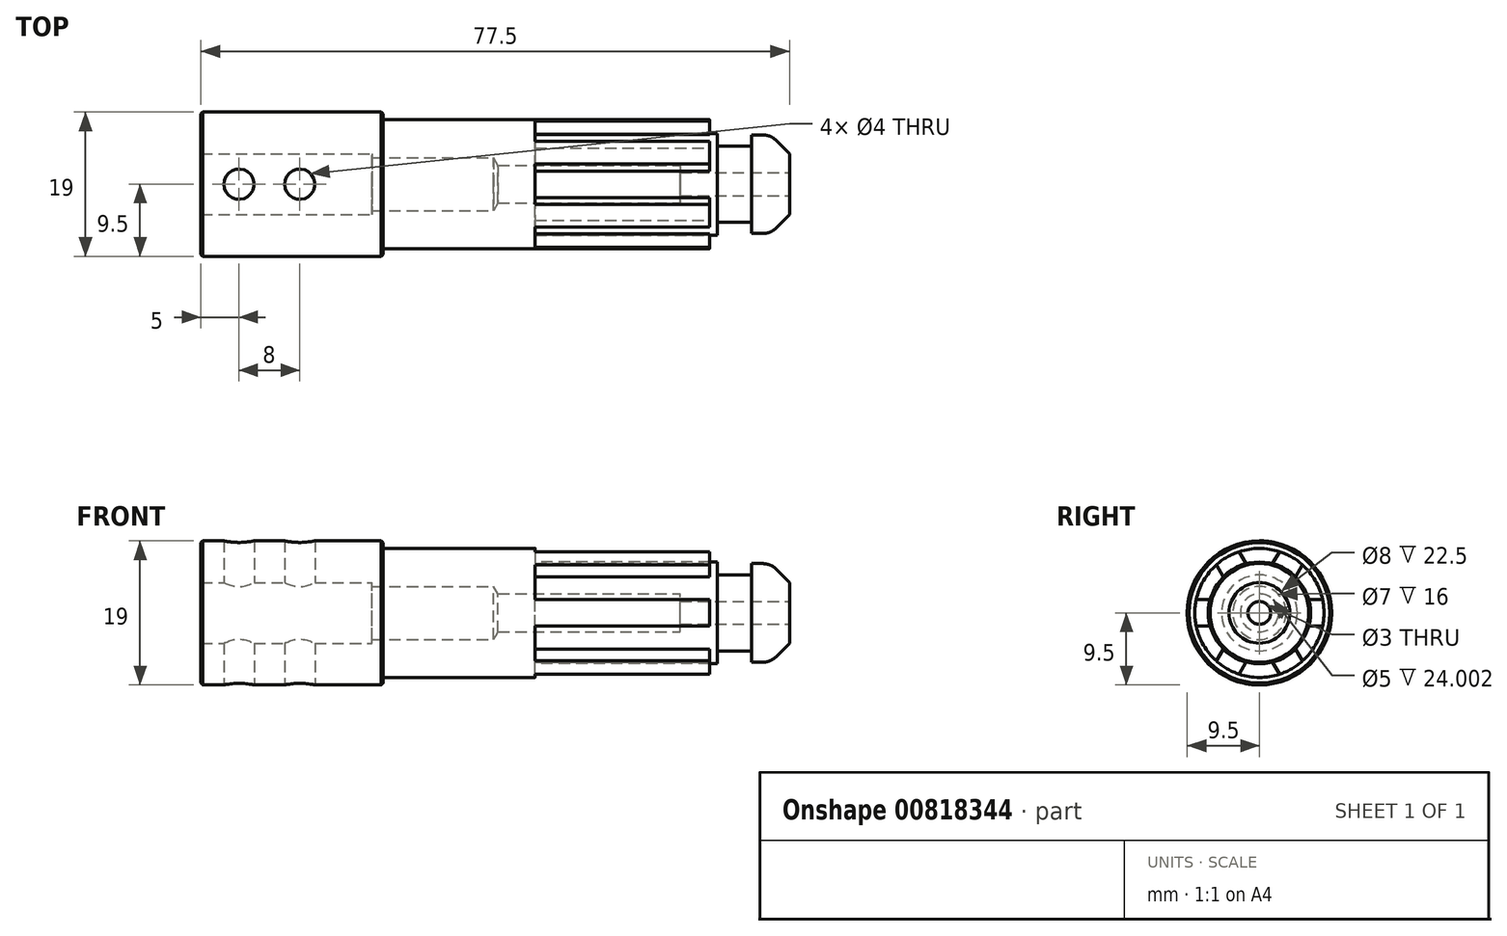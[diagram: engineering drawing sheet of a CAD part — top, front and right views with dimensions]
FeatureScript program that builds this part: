
annotation { "Feature Type Name" : "Feature", "Feature Type Description" : "" }
export const myFeature = defineFeature(function(context is Context, id is Id, definition is map)
    precondition{}
    {
        {
            var Q0;
            Q0=qCreatedBy(makeId("Right.planeOp"),FACE);
            var sketch = newSketch(context, id + "F0", { "sketchPlane" : qUnion([Q0])});
            skCircle(sketch, "E0", {"center": v(0, 0) * mm, "radius": 9.5 * mm});
            skSolve(sketch);
        }
        {
            var Q0;
            Q0=makeQuery(id+"F0.imprint","IMPRINT",FACE,{"disambiguationData":[TD([[makeQuery(id+"F0.imprint","IMPRINT",EDGE,{"derivedFrom":sQuery(id+"F0.wireOp",EDGE,"E0")}),1.0]])]});
            extrude(context, id + "F1", {"entities" : qUnion([Q0]), "depth" : 24 * mm, "offsetDistance" : 25 * mm});
        }
        {
            var Q0;
            Q0=makeQuery(id+"F1.opExtrude","CAP_FACE",FACE,{"disambiguationData":[OSD([sQuery(id+"F0.wireOp",EDGE,"E0")])],"isStart":false});
            var sketch = newSketch(context, id + "F2", { "sketchPlane" : qUnion([Q0])});
            skCircle(sketch, "E1", {"center": v(0, 0) * mm, "radius": 8.5 * mm});
            skSolve(sketch);
        }
        {
            var Q0;
            Q0=makeQuery(id+"F2.imprint","IMPRINT",FACE,{"disambiguationData":[TD([[makeQuery(id+"F2.imprint","IMPRINT",EDGE,{"derivedFrom":sQuery(id+"F2.wireOp",EDGE,"E1")}),1.0]])]});
            extrude(context, id + "F3", {"entities" : qUnion([Q0]), "operationType" : NewBodyOperationType.ADD, "depth" : 43 * mm, "offsetDistance" : 25 * mm});
        }
        {
            var Q0;
            Q0=makeQuery(id+"F3.opExtrude","CAP_FACE",FACE,{"disambiguationData":[OSD([sQuery(id+"F2.wireOp",EDGE,"E1")])],"isStart":false});
            var sketch = newSketch(context, id + "F4", { "sketchPlane" : qUnion([Q0])});
            skCircle(sketch, "E2", {"center": v(0, 0) * mm, "radius": 6.7 * mm});
            skSolve(sketch);
        }
        {
            var Q0;
            Q0=makeQuery(id+"F4.imprint","IMPRINT",FACE,{"disambiguationData":[TD([[makeQuery(id+"F4.imprint","IMPRINT",EDGE,{"derivedFrom":sQuery(id+"F4.wireOp",EDGE,"E2")}),1.0]])]});
            extrude(context, id + "F5", {"entities" : qUnion([Q0]), "operationType" : NewBodyOperationType.ADD, "depth" : 1 * mm, "offsetDistance" : 25 * mm});
        }
        {
            var Q0;
            Q0=makeQuery(id+"F5.opExtrude","CAP_FACE",FACE,{"disambiguationData":[OSD([sQuery(id+"F4.wireOp",EDGE,"E2")])],"isStart":false});
            var sketch = newSketch(context, id + "F6", { "sketchPlane" : qUnion([Q0])});
            skCircle(sketch, "E3", {"center": v(0, 0) * mm, "radius": 5 * mm});
            skSolve(sketch);
        }
        {
            var Q0;
            Q0=makeQuery(id+"F6.imprint","IMPRINT",FACE,{"disambiguationData":[TD([[makeQuery(id+"F6.imprint","IMPRINT",EDGE,{"derivedFrom":sQuery(id+"F6.wireOp",EDGE,"E3")}),1.0]])]});
            extrude(context, id + "F7", {"entities" : qUnion([Q0]), "operationType" : NewBodyOperationType.ADD, "depth" : 4.5 * mm, "offsetDistance" : 25 * mm});
        }
        {
            var Q0;
            Q0=makeQuery(id+"F7.opExtrude","CAP_FACE",FACE,{"disambiguationData":[OSD([sQuery(id+"F6.wireOp",EDGE,"E3")])],"isStart":false});
            var sketch = newSketch(context, id + "F8", { "sketchPlane" : qUnion([Q0])});
            skCircle(sketch, "E4", {"center": v(0, 0) * mm, "radius": 6.5 * mm});
            skSolve(sketch);
        }
        {
            var Q0;
            Q0=makeQuery(id+"F8.imprint","IMPRINT",FACE,{"disambiguationData":[TD([[makeQuery(id+"F8.imprint","IMPRINT",EDGE,{"derivedFrom":sQuery(id+"F8.wireOp",EDGE,"E4")}),1.0]])]});
            var Q1;
            Q1=makeQuery(id+"F8.imprint","IMPRINT",FACE,{"disambiguationData":[TD([[makeQuery(id+"F8.imprint","IMPRINT",EDGE,{"derivedFrom":makeQuery(id+"F7.opExtrude","CAP_EDGE",EDGE,{"disambiguationData":[OSD([sQuery(id+"F6.wireOp",EDGE,"E3")])],"isStart":false})}),1.0]])]});
            extrude(context, id + "F9", {"entities" : qUnion([Q0, Q1]), "operationType" : NewBodyOperationType.ADD, "depth" : 5 * mm, "offsetDistance" : 25 * mm});
        }
        {
            var Q0;
            Q0=makeQuery(id+"F9.opExtrude","CAP_EDGE",EDGE,{"disambiguationData":[OSD([sQuery(id+"F8.wireOp",EDGE,"E4")])],"isStart":false});
            chamfer(context, id + "F10", {"entities" : qUnion([Q0]), "width" : 2.5 * mm, "tangentPropagation" : true});
        }
        {
            var Q0;
            {var subQ0=sQuery(id+"F8.wireOp",EDGE,"E4");Q0=makeQuery(id+"F10.opChamfer","BLEND_EDGE",EDGE,{"blendedFrom":[makeQuery(id+"F9.opExtrude","CAP_EDGE",EDGE,{"disambiguationData":[OSD([subQ0])],"isStart":false}),makeQuery(id+"F9.opExtrude","SWEPT_FACE",FACE,{"disambiguationData":[OSD([subQ0])]})],"blendedInto":[makeQuery(id+"F9.opExtrude","SWEPT_FACE",FACE,{"disambiguationData":[OSD([subQ0])]})]});}
            fillet(context, id + "F11", {"entities" : qUnion([Q0]), "radius" : 2.5 * mm, "tangentPropagation" : true, "allowEdgeOverflow" : false});
        }
        {
            var Q0;
            Q0=makeQuery(id+"F3.opExtrude","CAP_FACE",FACE,{"disambiguationData":[OSD([sQuery(id+"F2.wireOp",EDGE,"E1")])],"isStart":false});
            var sketch = newSketch(context, id + "F12", { "sketchPlane" : qUnion([Q0])});
            skArc(sketch, "E5", {"start": v(-1.74, 6.52) * mm, "mid": v(-3.37, 5.85) * mm, "end": v(-4.78, 4.77) * mm});
            skLineSegment(sketch, "E6", {"start": v(9.02, 1.75) * mm, "end": v(6.52, 1.75) * mm});
            skLineSegment(sketch, "E7", {"start": v(9.02, -1.75) * mm, "end": v(6.47, -1.75) * mm});
            skLineSegment(sketch, "E8.1.0", {"start": v(3, 8.69) * mm, "end": v(1.74, 6.52) * mm});
            skLineSegment(sketch, "E8.1.3", {"start": v(6.03, 6.94) * mm, "end": v(4.75, 4.73) * mm});
            skLineSegment(sketch, "E8.2.0", {"start": v(-6.03, 6.94) * mm, "end": v(-4.78, 4.77) * mm});
            skLineSegment(sketch, "E8.2.3", {"start": v(-3, 8.69) * mm, "end": v(-1.72, 6.48) * mm});
            skLineSegment(sketch, "E8.3.0", {"start": v(-9.02, -1.75) * mm, "end": v(-6.52, -1.75) * mm});
            skLineSegment(sketch, "E8.3.3", {"start": v(-9.02, 1.75) * mm, "end": v(-6.47, 1.75) * mm});
            skLineSegment(sketch, "E8.4.0", {"start": v(-3, -8.69) * mm, "end": v(-1.74, -6.52) * mm});
            skLineSegment(sketch, "E8.4.3", {"start": v(-6.03, -6.94) * mm, "end": v(-4.75, -4.73) * mm});
            skLineSegment(sketch, "E8.5.0", {"start": v(6.03, -6.94) * mm, "end": v(4.78, -4.77) * mm});
            skLineSegment(sketch, "E8.5.3", {"start": v(3, -8.69) * mm, "end": v(1.72, -6.48) * mm});
            skLineSegment(sketch, "E9", {"start": v(-3, 8.69) * mm, "end": v(3, 8.69) * mm});
            skLineSegment(sketch, "E10", {"start": v(6.03, 6.94) * mm, "end": v(9.02, 1.75) * mm});
            skLineSegment(sketch, "E11", {"start": v(9.02, -1.75) * mm, "end": v(6.03, -6.94) * mm});
            skLineSegment(sketch, "E12", {"start": v(3, -8.69) * mm, "end": v(-3, -8.69) * mm});
            skLineSegment(sketch, "E13", {"start": v(-6.03, -6.94) * mm, "end": v(-9.02, -1.75) * mm});
            skLineSegment(sketch, "E14", {"start": v(-9.02, 1.75) * mm, "end": v(-6.03, 6.94) * mm});
            skArc(sketch, "E15.trimOffspring", {"start": v(4.78, 4.77) * mm, "mid": v(3.38, 5.85) * mm, "end": v(1.74, 6.52) * mm});
            skArc(sketch, "E16.trimOffspring", {"start": v(6.52, -1.75) * mm, "mid": v(6.75, 0) * mm, "end": v(6.52, 1.75) * mm});
            skArc(sketch, "E17.trimOffspring", {"start": v(1.74, -6.52) * mm, "mid": v(3.38, -5.85) * mm, "end": v(4.78, -4.77) * mm});
            skArc(sketch, "E18.trimOffspring", {"start": v(-4.78, -4.77) * mm, "mid": v(-3.38, -5.85) * mm, "end": v(-1.74, -6.52) * mm});
            skArc(sketch, "E19.trimOffspring", {"start": v(-6.52, 1.75) * mm, "mid": v(-6.75, 0) * mm, "end": v(-6.52, -1.75) * mm});
            skSolve(sketch);
        }
        {
            var Q0;
            {var subQ5=sQuery(id+"F12.wireOp",EDGE,"E5");Q0=makeQuery(id+"F12.imprint","IMPRINT",FACE,{"disambiguationData":[TD([[makeQuery(id+"F12.imprint","IMPRINT",EDGE,{"derivedFrom":subQ5}),1.0]])]});}
            var Q1;
            {var subQ10=sQuery(id+"F12.wireOp",EDGE,"E19.trimOffspring");Q1=makeQuery(id+"F12.imprint","IMPRINT",FACE,{"disambiguationData":[TD([[makeQuery(id+"F12.imprint","IMPRINT",EDGE,{"derivedFrom":subQ10}),1.0]])]});}
            var Q2;
            {var subQ4=sQuery(id+"F12.wireOp",EDGE,"E18.trimOffspring");Q2=makeQuery(id+"F12.imprint","IMPRINT",FACE,{"disambiguationData":[TD([[makeQuery(id+"F12.imprint","IMPRINT",EDGE,{"derivedFrom":subQ4}),1.0]])]});}
            var Q3;
            {var subQ10=sQuery(id+"F12.wireOp",EDGE,"E16.trimOffspring");Q3=makeQuery(id+"F12.imprint","IMPRINT",FACE,{"disambiguationData":[TD([[makeQuery(id+"F12.imprint","IMPRINT",EDGE,{"derivedFrom":subQ10}),1.0]])]});}
            var Q4;
            {var subQ6=sQuery(id+"F12.wireOp",EDGE,"E15.trimOffspring");Q4=makeQuery(id+"F12.imprint","IMPRINT",FACE,{"disambiguationData":[TD([[makeQuery(id+"F12.imprint","IMPRINT",EDGE,{"derivedFrom":subQ6}),1.0]])]});}
            var Q5;
            {var subQ0=sQuery(id+"F12.wireOp",EDGE,"E14");Q5=makeQuery(id+"F12.imprint","IMPRINT",FACE,{"disambiguationData":[TD([[makeQuery(id+"F12.imprint","IMPRINT",EDGE,{"derivedFrom":subQ0}),-1.0]])]});}
            var Q6;
            {var subQ0=sQuery(id+"F12.wireOp",EDGE,"E9");Q6=makeQuery(id+"F12.imprint","IMPRINT",FACE,{"disambiguationData":[TD([[makeQuery(id+"F12.imprint","IMPRINT",EDGE,{"derivedFrom":subQ0}),-1.0]])]});}
            var Q7;
            {var subQ0=sQuery(id+"F12.wireOp",EDGE,"E10");Q7=makeQuery(id+"F12.imprint","IMPRINT",FACE,{"disambiguationData":[TD([[makeQuery(id+"F12.imprint","IMPRINT",EDGE,{"derivedFrom":subQ0}),-1.0]])]});}
            var Q8;
            {var subQ0=sQuery(id+"F12.wireOp",EDGE,"E13");Q8=makeQuery(id+"F12.imprint","IMPRINT",FACE,{"disambiguationData":[TD([[makeQuery(id+"F12.imprint","IMPRINT",EDGE,{"derivedFrom":subQ0}),-1.0]])]});}
            var Q9;
            {var subQ0=sQuery(id+"F12.wireOp",EDGE,"E12");Q9=makeQuery(id+"F12.imprint","IMPRINT",FACE,{"disambiguationData":[TD([[makeQuery(id+"F12.imprint","IMPRINT",EDGE,{"derivedFrom":subQ0}),-1.0]])]});}
            var Q10;
            {var subQ0=sQuery(id+"F12.wireOp",EDGE,"E17.trimOffspring");Q10=makeQuery(id+"F12.imprint","IMPRINT",FACE,{"disambiguationData":[TD([[makeQuery(id+"F12.imprint","IMPRINT",EDGE,{"derivedFrom":subQ0}),1.0]])]});}
            var Q11;
            {var subQ0=sQuery(id+"F12.wireOp",EDGE,"E11");Q11=makeQuery(id+"F12.imprint","IMPRINT",FACE,{"disambiguationData":[TD([[makeQuery(id+"F12.imprint","IMPRINT",EDGE,{"derivedFrom":subQ0}),-1.0]])]});}
            extrude(context, id + "F13", {"entities" : qUnion([Q0, Q1, Q2, Q3, Q4, Q5, Q6, Q7, Q8, Q9, Q10, Q11]), "operationType" : NewBodyOperationType.REMOVE, "oppositeDirection" : true, "depth" : 23 * mm, "offsetDistance" : 25 * mm});
        }
        {
            var Q0;
            Q0=sQuery(id+"F0.wireOp",VERTEX,"E0.center");
            var Q1;
            Q1=makeQuery(id+"F1.opExtrude","SWEPT_BODY",BODY,{"disambiguationData":[OSD([sQuery(id+"F0.wireOp",EDGE,"E0")])]});
            hole(context, id + "F14", {"style" : HoleStyle.C_BORE, "endStyle" : HoleEndStyle.BLIND, "oppositeDirection" : true, "holeDiameter" : 7 * mm, "cBoreDiameter" : 8 * mm, "cBoreDepth" : 22.5 * mm, "majorDiameter" : 5 * mm, "holeDepth" : 38.5 * mm, "isTappedThrough" : true, "tappedDepth" : 12 * mm, "tapClearance" : 3, "locations" : qUnion([Q0]), "scope" : qUnion([Q1])});
        }
        {
            var Q0;
            Q0=sQuery(id+"F0.wireOp",VERTEX,"E0.center");
            var Q1;
            Q1=makeQuery(id+"F1.opExtrude","SWEPT_BODY",BODY,{"disambiguationData":[OSD([sQuery(id+"F0.wireOp",EDGE,"E0")])]});
            hole(context, id + "F15", {"style" : HoleStyle.C_BORE, "endStyle" : HoleEndStyle.THROUGH, "oppositeDirection" : true, "holeDiameter" : 3 * mm, "cBoreDiameter" : 5 * mm, "cBoreDepth" : 22.5 * mm, "majorDiameter" : 5 * mm, "isTappedThrough" : true, "tappedDepth" : 12 * mm, "tapClearance" : 3, "locations" : qUnion([Q0]), "scope" : qUnion([Q1])});
        }
        {
            var Q0;
            Q0=qCreatedBy(makeId("Top.planeOp"),FACE);
            cPlane(context, id + "F16", {"entities" : qUnion([Q0]), "cplaneType" : CPlaneType.OFFSET, "offset" : 10 * mm, "width" : 150 * mm, "height" : 150 * mm});
        }
        {
            var Q0;
            Q0=qCreatedBy(id+"F16.planeOp",FACE);
            var sketch = newSketch(context, id + "F17", { "sketchPlane" : qUnion([Q0])});
            skPoint(sketch, "E20", {"position": v(5, 0) * mm});
            skPoint(sketch, "E21", {"position": v(13, 0) * mm});
            skSolve(sketch);
        }
        {
            var Q0;
            Q0=sQuery(id+"F17.wireOp",VERTEX,"E20");
            var Q1;
            Q1=sQuery(id+"F17.wireOp",VERTEX,"E21");
            var Q2;
            Q2=makeQuery(id+"F1.opExtrude","SWEPT_BODY",BODY,{"disambiguationData":[OSD([sQuery(id+"F0.wireOp",EDGE,"E0")])]});
            hole(context, id + "F18", {"style" : HoleStyle.SIMPLE, "endStyle" : HoleEndStyle.THROUGH, "holeDiameter" : 4 * mm, "majorDiameter" : 5 * mm, "isTappedThrough" : true, "tappedDepth" : 12 * mm, "tapClearance" : 3, "locations" : qUnion([Q0, Q1]), "scope" : qUnion([Q2])});
        }
        {
            var Q0;
            Q0=makeQuery(id+"F18.hole-1.boolean.opBoolean","INTERSECT",EDGE,{"disambiguationData":[OD(0.0)],"derivedFrom":[makeQuery(id+"F1.opExtrude","SWEPT_FACE",FACE,{"disambiguationData":[OSD([sQuery(id+"F0.wireOp",EDGE,"E0")])]}),makeQuery(id+"F18.hole-1.opRevolve","SWEPT_FACE",FACE,{"disambiguationData":[OSD([sQuery(id+"F18.hole-1.sketch.wireOp",EDGE,"core_line_2")])]})]});
            var Q1;
            Q1=makeQuery(id+"F18.hole-0.boolean.opBoolean","INTERSECT",EDGE,{"disambiguationData":[OD(0.0)],"derivedFrom":[makeQuery(id+"F1.opExtrude","SWEPT_FACE",FACE,{"disambiguationData":[OSD([sQuery(id+"F0.wireOp",EDGE,"E0")])]}),makeQuery(id+"F18.hole-0.opRevolve","SWEPT_FACE",FACE,{"disambiguationData":[OSD([sQuery(id+"F18.hole-0.sketch.wireOp",EDGE,"core_line_2")])]})]});
            var Q2;
            Q2=makeQuery(id+"F18.hole-0.boolean.opBoolean","INTERSECT",EDGE,{"disambiguationData":[OD(1.0)],"derivedFrom":[makeQuery(id+"F1.opExtrude","SWEPT_FACE",FACE,{"disambiguationData":[OSD([sQuery(id+"F0.wireOp",EDGE,"E0")])]}),makeQuery(id+"F18.hole-0.opRevolve","SWEPT_FACE",FACE,{"disambiguationData":[OSD([sQuery(id+"F18.hole-0.sketch.wireOp",EDGE,"core_line_2")])]})]});
            var Q3;
            Q3=makeQuery(id+"F18.hole-1.boolean.opBoolean","INTERSECT",EDGE,{"disambiguationData":[OD(1.0)],"derivedFrom":[makeQuery(id+"F1.opExtrude","SWEPT_FACE",FACE,{"disambiguationData":[OSD([sQuery(id+"F0.wireOp",EDGE,"E0")])]}),makeQuery(id+"F18.hole-1.opRevolve","SWEPT_FACE",FACE,{"disambiguationData":[OSD([sQuery(id+"F18.hole-1.sketch.wireOp",EDGE,"core_line_2")])]})]});
            var Q4;
            Q4=makeQuery(id+"F1.opExtrude","CAP_EDGE",EDGE,{"disambiguationData":[OSD([sQuery(id+"F0.wireOp",EDGE,"E0")])],"isStart":false});
            var Q5;
            Q5=makeQuery(id+"F1.opExtrude","CAP_EDGE",EDGE,{"disambiguationData":[OSD([sQuery(id+"F0.wireOp",EDGE,"E0")])],"isStart":true});
            var Q6;
            Q6=makeQuery(id+"F14.hole-0.boolean.opBoolean","COPY",EDGE,{"derivedFrom":makeQuery(id+"F14.hole-0.opRevolve","SWEPT_EDGE",EDGE,{"disambiguationData":[OSD([sQuery(id+"F14.hole-0.sketch.wireOp",EDGE,"cbore_start_line_2"),sQuery(id+"F14.hole-0.sketch.wireOp",EDGE,"cbore_start_line_3")])]})});
            var Q7;
            Q7=makeQuery(id+"F15.hole-0.boolean.opBoolean","INTERSECT",EDGE,{"derivedFrom":[makeQuery(id+"F9.opExtrude","CAP_FACE",FACE,{"disambiguationData":[OSD([sQuery(id+"F8.wireOp",EDGE,"E4")])],"isStart":false}),makeQuery(id+"F15.hole-0.opRevolve","SWEPT_FACE",FACE,{"disambiguationData":[OSD([sQuery(id+"F15.hole-0.sketch.wireOp",EDGE,"core_line_2")])]})]});
            chamfer(context, id + "F19", {"entities" : qUnion([Q0, Q1, Q2, Q3, Q4, Q5, Q6, Q7]), "width" : 0.25 * mm, "tangentPropagation" : true});
        }
    });
